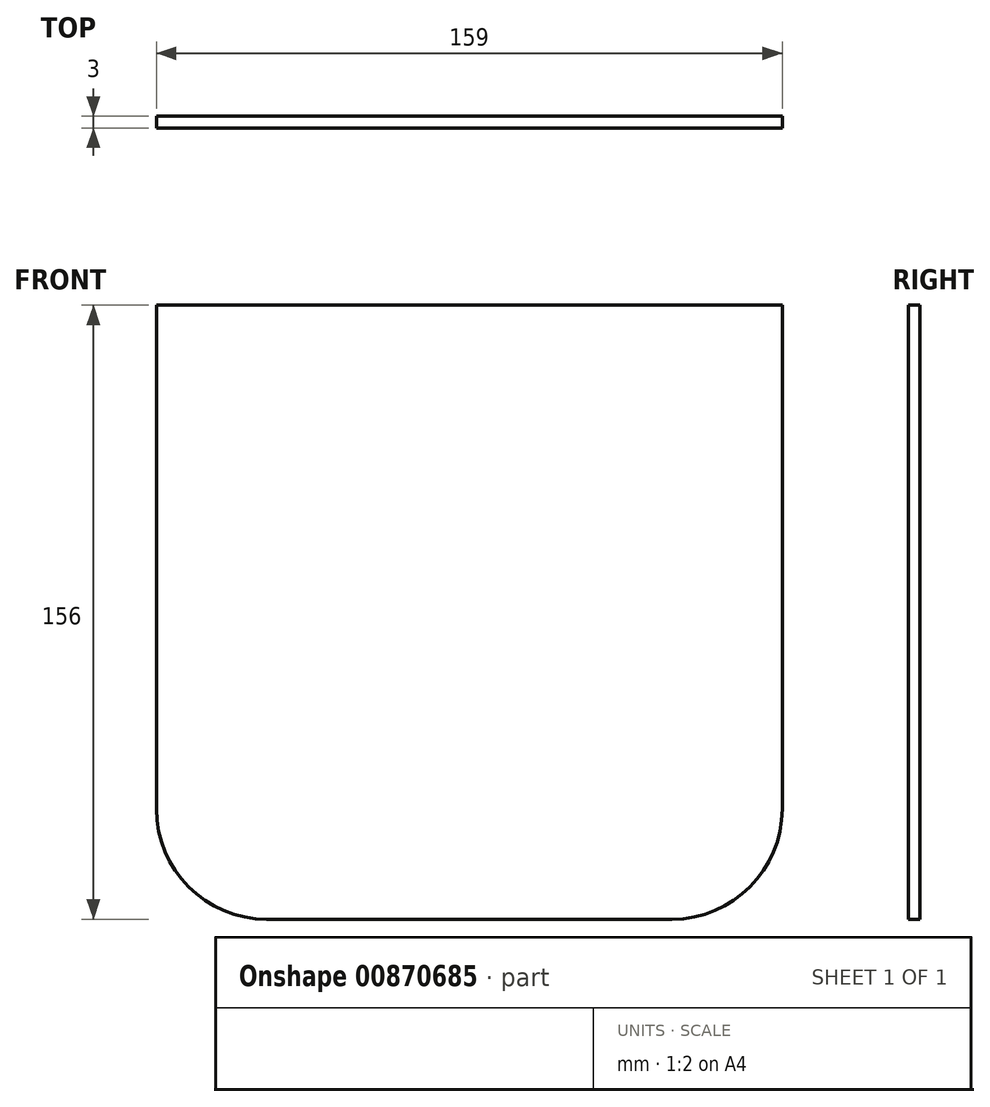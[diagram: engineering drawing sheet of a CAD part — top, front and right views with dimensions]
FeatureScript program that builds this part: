
annotation { "Feature Type Name" : "Feature", "Feature Type Description" : "" }
export const myFeature = defineFeature(function(context is Context, id is Id, definition is map)
    precondition{}
    {
        {
            var Q0;
            Q0=qCreatedBy(makeId("Front.planeOp"),FACE);
            var sketch = newSketch(context, id + "F0", { "sketchPlane" : qUnion([Q0])});
            skLineSegment(sketch, "E0.bottom", {"start": v(79.5, 78) * mm, "end": v(-79.5, 78) * mm});
            skLineSegment(sketch, "E0.top", {"start": v(51.5, -78) * mm, "end": v(-51.5, -78) * mm});
            skLineSegment(sketch, "E0.left", {"start": v(79.5, 78) * mm, "end": v(79.5, -50) * mm});
            skLineSegment(sketch, "E0.right", {"start": v(-79.5, 78) * mm, "end": v(-79.5, -50) * mm});
            skPoint(sketch, "E0.middle", {"position": v(0, 0) * mm});
            skPoint(sketch, "E1.visualSharp", {"position": v(-79.5, -78) * mm});
            skArc(sketch, "E1.filletArc", {"start": v(-79.5, -50) * mm, "mid": v(-71.3, -69.8) * mm, "end": v(-51.5, -78) * mm});
            skPoint(sketch, "E2.visualSharp", {"position": v(79.5, -78) * mm});
            skArc(sketch, "E2.filletArc", {"start": v(51.5, -78) * mm, "mid": v(71.3, -69.8) * mm, "end": v(79.5, -50) * mm});
            skSolve(sketch);
        }
        {
            var Q0;
            Q0=makeQuery(id+"F0.imprint","IMPRINT",FACE,{"disambiguationData":[TD([[makeQuery(id+"F0.imprint","IMPRINT",EDGE,{"derivedFrom":sQuery(id+"F0.wireOp",EDGE,"E0.bottom")}),1.0]])]});
            extrude(context, id + "F1", {"entities" : qUnion([Q0]), "depth" : 3 * mm, "offsetDistance" : 25 * mm});
        }
    });
